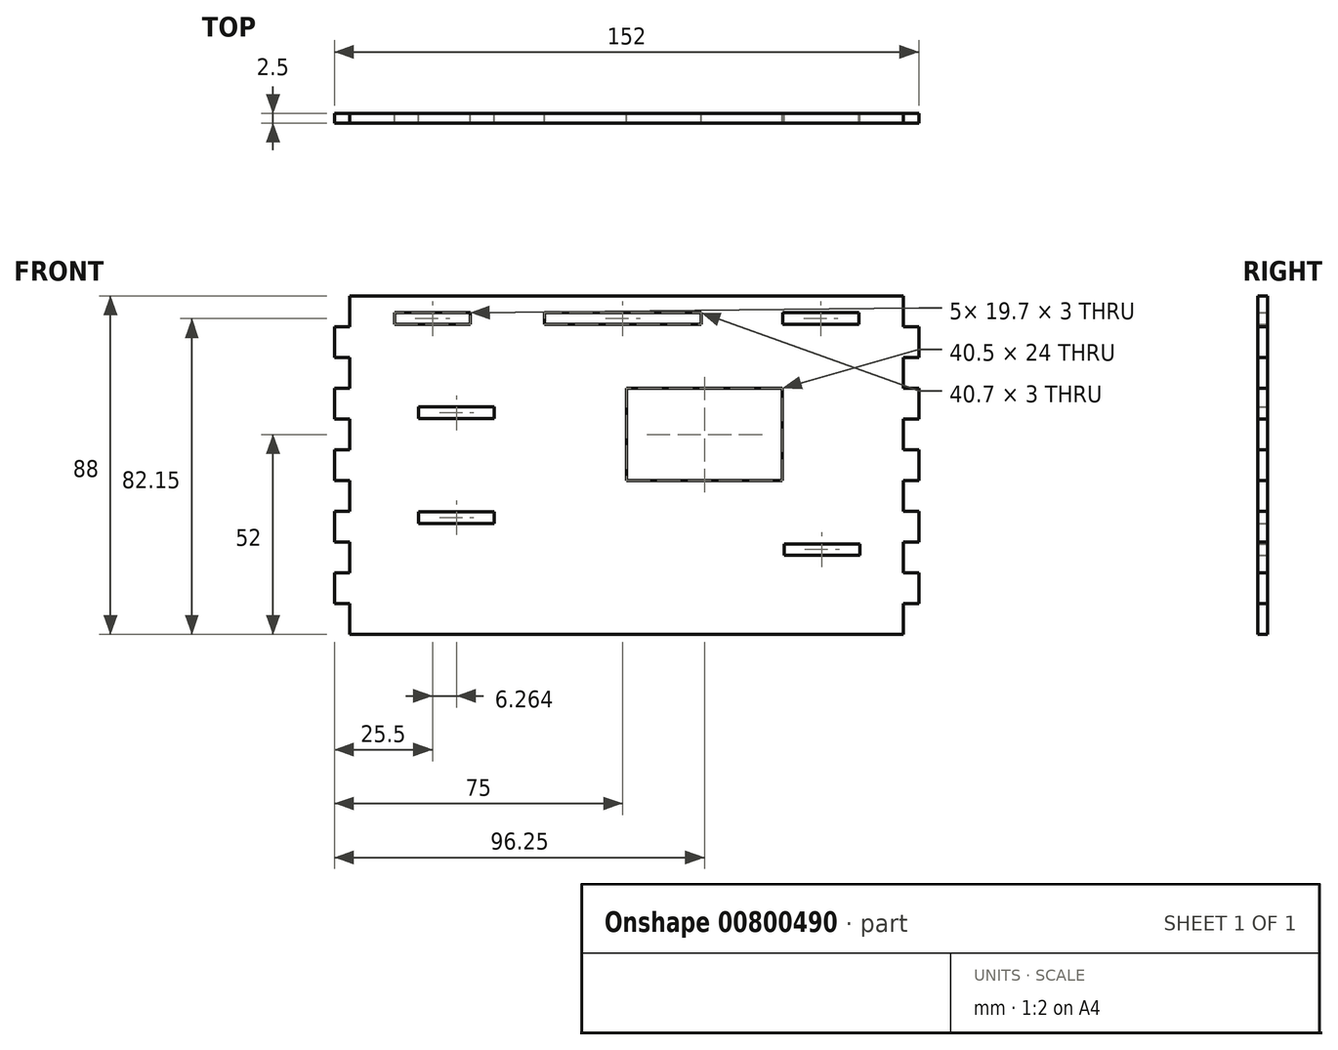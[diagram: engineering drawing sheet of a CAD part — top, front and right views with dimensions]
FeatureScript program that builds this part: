
annotation { "Feature Type Name" : "Feature", "Feature Type Description" : "" }
export const myFeature = defineFeature(function(context is Context, id is Id, definition is map)
    precondition{}
    {
        {
            var Q0;
            Q0=qCreatedBy(makeId("Front.planeOp"),FACE);
            var sketch = newSketch(context, id + "F0", { "sketchPlane" : qUnion([Q0])});
            skLineSegment(sketch, "E0.bottom", {"start": v(-72, 44) * mm, "end": v(72, 44) * mm});
            skLineSegment(sketch, "E0.top", {"start": v(-72, -44) * mm, "end": v(72, -44) * mm});
            skLineSegment(sketch, "E0.left", {"start": v(-72, 44) * mm, "end": v(-72, -44) * mm});
            skLineSegment(sketch, "E0.right", {"start": v(72, 44) * mm, "end": v(72, -44) * mm});
            skPoint(sketch, "E0.middle", {"position": v(0, 0) * mm});
            skLineSegment(sketch, "E1", {"start": v(-72, -44) * mm, "end": v(-72, -36) * mm});
            skLineSegment(sketch, "E2", {"start": v(-72, -36) * mm, "end": v(-76, -36) * mm});
            skLineSegment(sketch, "E3", {"start": v(-76, -36) * mm, "end": v(-76, -28) * mm});
            skLineSegment(sketch, "E4", {"start": v(-76, -28) * mm, "end": v(-72, -28) * mm});
            skLineSegment(sketch, "E5", {"start": v(-72, -28) * mm, "end": v(-72, -20) * mm});
            skLineSegment(sketch, "E6", {"start": v(-72, -20) * mm, "end": v(-76, -20) * mm});
            skLineSegment(sketch, "E7", {"start": v(-76, -20) * mm, "end": v(-76, -12) * mm});
            skLineSegment(sketch, "E8", {"start": v(-76, -12) * mm, "end": v(-72, -12) * mm});
            skLineSegment(sketch, "E9.MirrorCS", {"start": v(-76, 12) * mm, "end": v(-72, 12) * mm});
            skLineSegment(sketch, "E10.MirrorCS", {"start": v(-76, 20) * mm, "end": v(-76, 12) * mm});
            skLineSegment(sketch, "E11.MirrorCS", {"start": v(-72, 20) * mm, "end": v(-76, 20) * mm});
            skLineSegment(sketch, "E12.MirrorCS", {"start": v(-76, 28) * mm, "end": v(-72, 28) * mm});
            skLineSegment(sketch, "E13.MirrorCS", {"start": v(-76, 36) * mm, "end": v(-76, 28) * mm});
            skLineSegment(sketch, "E14.MirrorCS", {"start": v(-72, 36) * mm, "end": v(-76, 36) * mm});
            skLineSegment(sketch, "E15", {"start": v(-72, -12) * mm, "end": v(-72, -4) * mm});
            skLineSegment(sketch, "E16", {"start": v(-72, -4) * mm, "end": v(-76, -4) * mm});
            skLineSegment(sketch, "E17", {"start": v(-76, -4) * mm, "end": v(-76, 4) * mm});
            skLineSegment(sketch, "E18", {"start": v(-76, 4) * mm, "end": v(-72, 4) * mm});
            skLineSegment(sketch, "E19.MirrorCS", {"start": v(72, 36) * mm, "end": v(76, 36) * mm});
            skLineSegment(sketch, "E20.MirrorCS", {"start": v(76, 36) * mm, "end": v(76, 28) * mm});
            skLineSegment(sketch, "E21.MirrorCS", {"start": v(76, 28) * mm, "end": v(72, 28) * mm});
            skLineSegment(sketch, "E22.MirrorCS", {"start": v(72, 20) * mm, "end": v(76, 20) * mm});
            skLineSegment(sketch, "E23.MirrorCS", {"start": v(76, 20) * mm, "end": v(76, 12) * mm});
            skLineSegment(sketch, "E24.MirrorCS", {"start": v(76, 12) * mm, "end": v(72, 12) * mm});
            skLineSegment(sketch, "E25.MirrorCS", {"start": v(76, 4) * mm, "end": v(72, 4) * mm});
            skLineSegment(sketch, "E26.MirrorCS", {"start": v(76, -4) * mm, "end": v(76, 4) * mm});
            skLineSegment(sketch, "E27.MirrorCS", {"start": v(72, -4) * mm, "end": v(76, -4) * mm});
            skLineSegment(sketch, "E28.MirrorCS", {"start": v(76, -12) * mm, "end": v(72, -12) * mm});
            skLineSegment(sketch, "E29.MirrorCS", {"start": v(76, -20) * mm, "end": v(76, -12) * mm});
            skLineSegment(sketch, "E30.MirrorCS", {"start": v(72, -20) * mm, "end": v(76, -20) * mm});
            skLineSegment(sketch, "E31.MirrorCS", {"start": v(76, -28) * mm, "end": v(72, -28) * mm});
            skLineSegment(sketch, "E32.MirrorCS", {"start": v(76, -36) * mm, "end": v(76, -28) * mm});
            skLineSegment(sketch, "E33.MirrorCS", {"start": v(72, -36) * mm, "end": v(76, -36) * mm});
            skPoint(sketch, "E34.endSnap0", {"position": v(-74, 20) * mm});
            skLineSegment(sketch, "E35", {"start": v(40.5, -4) * mm, "end": v(40.5, 20) * mm});
            skLineSegment(sketch, "E36", {"start": v(40.5, 20) * mm, "end": v(0, 20) * mm});
            skLineSegment(sketch, "E37", {"start": v(0, 20) * mm, "end": v(0, -4) * mm});
            skLineSegment(sketch, "E38", {"start": v(0, -4) * mm, "end": v(40.5, -4) * mm});
            skPoint(sketch, "E39.middle", {"position": v(-50.5, 38.15) * mm});
            skPoint(sketch, "E40.middle", {"position": v(-44.24, 13.65) * mm});
            skPoint(sketch, "E41.middle", {"position": v(50.81, -21.94) * mm});
            skLineSegment(sketch, "E42", {"start": v(-72, 44) * mm, "end": v(-1, 44) * mm});
            skPoint(sketch, "E43.middle", {"position": v(-1, 38.15) * mm});
            skLineSegment(sketch, "E44.bottom", {"start": v(-40.65, 36.65) * mm, "end": v(-60.35, 36.65) * mm});
            skLineSegment(sketch, "E44.top", {"start": v(-40.65, 39.65) * mm, "end": v(-60.35, 39.65) * mm});
            skLineSegment(sketch, "E44.left", {"start": v(-40.65, 36.65) * mm, "end": v(-40.65, 39.65) * mm});
            skLineSegment(sketch, "E44.right", {"start": v(-60.35, 36.65) * mm, "end": v(-60.35, 39.65) * mm});
            skLineSegment(sketch, "E45.bottom", {"start": v(-34.39, 12.15) * mm, "end": v(-54.09, 12.15) * mm});
            skLineSegment(sketch, "E45.top", {"start": v(-34.39, 15.15) * mm, "end": v(-54.09, 15.15) * mm});
            skLineSegment(sketch, "E45.left", {"start": v(-34.39, 12.15) * mm, "end": v(-34.39, 15.15) * mm});
            skLineSegment(sketch, "E45.right", {"start": v(-54.09, 12.15) * mm, "end": v(-54.09, 15.15) * mm});
            skLineSegment(sketch, "E46.bottom", {"start": v(60.66, -23.44) * mm, "end": v(40.96, -23.44) * mm});
            skLineSegment(sketch, "E46.top", {"start": v(60.66, -20.44) * mm, "end": v(40.96, -20.44) * mm});
            skLineSegment(sketch, "E46.left", {"start": v(60.66, -23.44) * mm, "end": v(60.66, -20.44) * mm});
            skLineSegment(sketch, "E46.right", {"start": v(40.96, -23.44) * mm, "end": v(40.96, -20.44) * mm});
            skLineSegment(sketch, "E47.bottom", {"start": v(19.35, 36.65) * mm, "end": v(-21.35, 36.65) * mm});
            skLineSegment(sketch, "E47.top", {"start": v(19.35, 39.65) * mm, "end": v(-21.35, 39.65) * mm});
            skLineSegment(sketch, "E47.left", {"start": v(19.35, 36.65) * mm, "end": v(19.35, 39.65) * mm});
            skLineSegment(sketch, "E47.right", {"start": v(-21.35, 36.65) * mm, "end": v(-21.35, 39.65) * mm});
            skLineSegment(sketch, "E48.MirrorCS", {"start": v(60.35, 36.65) * mm, "end": v(60.35, 39.65) * mm});
            skLineSegment(sketch, "E49.MirrorCS", {"start": v(40.65, 36.65) * mm, "end": v(40.65, 39.65) * mm});
            skPoint(sketch, "E50.MirrorP", {"position": v(50.5, 38.15) * mm});
            skLineSegment(sketch, "E51.MirrorCS", {"start": v(40.65, 36.65) * mm, "end": v(60.35, 36.65) * mm});
            skLineSegment(sketch, "E52.MirrorCS", {"start": v(40.65, 39.65) * mm, "end": v(60.35, 39.65) * mm});
            skLineSegment(sketch, "E53.MirrorCS", {"start": v(-34.39, -12.15) * mm, "end": v(-34.39, -15.15) * mm});
            skLineSegment(sketch, "E54.MirrorCS", {"start": v(-54.09, -12.15) * mm, "end": v(-54.09, -15.15) * mm});
            skPoint(sketch, "E55.MirrorP", {"position": v(-44.24, -13.65) * mm});
            skLineSegment(sketch, "E56.MirrorCS", {"start": v(-34.39, -12.15) * mm, "end": v(-54.09, -12.15) * mm});
            skLineSegment(sketch, "E57.MirrorCS", {"start": v(-34.39, -15.15) * mm, "end": v(-54.09, -15.15) * mm});
            skSolve(sketch);
        }
        {
            var Q0;
            {var subQ0=sQuery(id+"F0.wireOp",EDGE,"E28.MirrorCS");Q0=makeQuery(id+"F0.imprint","IMPRINT",FACE,{"disambiguationData":[TD([[makeQuery(id+"F0.imprint","IMPRINT",EDGE,{"derivedFrom":subQ0}),1.0]])]});}
            var Q1;
            {var subQ0=sQuery(id+"F0.wireOp",EDGE,"E31.MirrorCS");Q1=makeQuery(id+"F0.imprint","IMPRINT",FACE,{"disambiguationData":[TD([[makeQuery(id+"F0.imprint","IMPRINT",EDGE,{"derivedFrom":subQ0}),1.0]])]});}
            var Q2;
            {var subQ19=sQuery(id+"F0.wireOp",EDGE,"E0.top");Q2=makeQuery(id+"F0.imprint","IMPRINT",FACE,{"disambiguationData":[TD([[makeQuery(id+"F0.imprint","IMPRINT",EDGE,{"derivedFrom":subQ19}),1.0]])]});}
            var Q3;
            {var subQ0=sQuery(id+"F0.wireOp",EDGE,"E25.MirrorCS");Q3=makeQuery(id+"F0.imprint","IMPRINT",FACE,{"disambiguationData":[TD([[makeQuery(id+"F0.imprint","IMPRINT",EDGE,{"derivedFrom":subQ0}),1.0]])]});}
            var Q4;
            {var subQ0=sQuery(id+"F0.wireOp",EDGE,"E22.MirrorCS");Q4=makeQuery(id+"F0.imprint","IMPRINT",FACE,{"disambiguationData":[TD([[makeQuery(id+"F0.imprint","IMPRINT",EDGE,{"derivedFrom":subQ0}),-1.0]])]});}
            var Q5;
            {var subQ0=sQuery(id+"F0.wireOp",EDGE,"E19.MirrorCS");Q5=makeQuery(id+"F0.imprint","IMPRINT",FACE,{"disambiguationData":[TD([[makeQuery(id+"F0.imprint","IMPRINT",EDGE,{"derivedFrom":subQ0}),-1.0]])]});}
            var Q6;
            {var subQ0=sQuery(id+"F0.wireOp",EDGE,"E2");Q6=makeQuery(id+"F0.imprint","IMPRINT",FACE,{"disambiguationData":[TD([[makeQuery(id+"F0.imprint","IMPRINT",EDGE,{"derivedFrom":subQ0}),-1.0]])]});}
            var Q7;
            {var subQ0=sQuery(id+"F0.wireOp",EDGE,"E6");Q7=makeQuery(id+"F0.imprint","IMPRINT",FACE,{"disambiguationData":[TD([[makeQuery(id+"F0.imprint","IMPRINT",EDGE,{"derivedFrom":subQ0}),-1.0]])]});}
            var Q8;
            {var subQ0=sQuery(id+"F0.wireOp",EDGE,"E16");Q8=makeQuery(id+"F0.imprint","IMPRINT",FACE,{"disambiguationData":[TD([[makeQuery(id+"F0.imprint","IMPRINT",EDGE,{"derivedFrom":subQ0}),-1.0]])]});}
            var Q9;
            {var subQ0=sQuery(id+"F0.wireOp",EDGE,"E12.MirrorCS");Q9=makeQuery(id+"F0.imprint","IMPRINT",FACE,{"disambiguationData":[TD([[makeQuery(id+"F0.imprint","IMPRINT",EDGE,{"derivedFrom":subQ0}),1.0]])]});}
            var Q10;
            {var subQ0=sQuery(id+"F0.wireOp",EDGE,"E9.MirrorCS");Q10=makeQuery(id+"F0.imprint","IMPRINT",FACE,{"disambiguationData":[TD([[makeQuery(id+"F0.imprint","IMPRINT",EDGE,{"derivedFrom":subQ0}),1.0]])]});}
            extrude(context, id + "F1", {"entities" : qUnion([Q0, Q1, Q2, Q3, Q4, Q5, Q6, Q7, Q8, Q9, Q10]), "depth" : 2.5 * mm, "offsetDistance" : 25 * mm});
        }
    });
